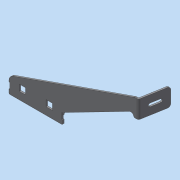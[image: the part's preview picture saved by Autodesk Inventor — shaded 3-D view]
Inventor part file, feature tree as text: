
AUTODESK INVENTOR PART (.ipt)
format: ipt  version: 2020 (Build 240168000, 168)  size: 230,400 bytes
history: native  units: mm
features: other x2, extrude x1, plane x1
ambient origin geometry x8: Origin, YZ Plane, XZ Plane, XY Plane, X Axis, Y Axis, Z Axis, Center Point
bodies: Body1 (feature_tree)
feature tree (4):
  other  "實體1"
  extrude  "擠出1"  Depth=130.0mm
  other  "折彎零件1"
  plane  "工作平面1"
